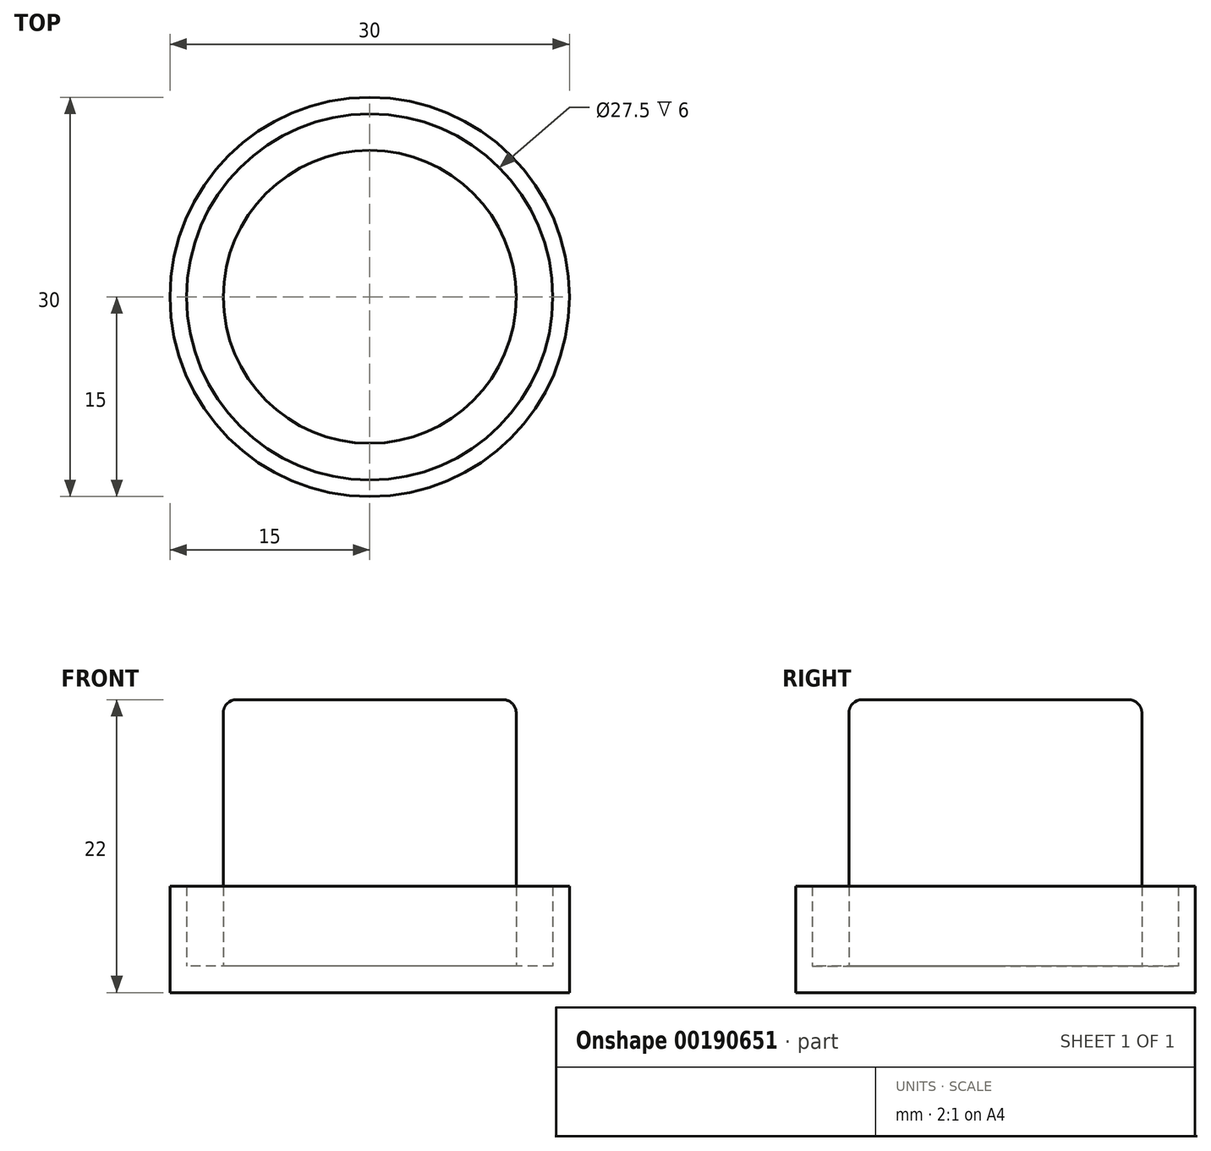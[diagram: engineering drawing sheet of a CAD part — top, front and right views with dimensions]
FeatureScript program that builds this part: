
annotation { "Feature Type Name" : "Feature", "Feature Type Description" : "" }
export const myFeature = defineFeature(function(context is Context, id is Id, definition is map)
    precondition{}
    {
        {
            var Q0;
            Q0=qCreatedBy(makeId("Top.planeOp"),FACE);
            var sketch = newSketch(context, id + "F0", { "sketchPlane" : qUnion([Q0])});
            skCircle(sketch, "E0", {"center": v(0, 0) * mm, "radius": 11 * mm});
            skCircle(sketch, "E1", {"center": v(0, 0) * mm, "radius": 13.75 * mm});
            skCircle(sketch, "E2", {"center": v(0, 0) * mm, "radius": 15 * mm});
            skSolve(sketch);
        }
        {
            var Q0;
            Q0=makeQuery(id+"F0.imprint","IMPRINT",FACE,{"disambiguationData":[TD([[makeQuery(id+"F0.imprint","IMPRINT",EDGE,{"derivedFrom":sQuery(id+"F0.wireOp",EDGE,"E1")}),-1.0]])]});
            extrude(context, id + "F1", {"entities" : qUnion([Q0]), "depth" : 6 * mm});
        }
        {
            var Q0;
            Q0 = qSketchRegion(id + "F0", true);
            var Q1;
            Q1=makeQuery(id+"F0.imprint","IMPRINT",FACE,{"disambiguationData":[TD([[makeQuery(id+"F0.imprint","IMPRINT",EDGE,{"derivedFrom":sQuery(id+"F0.wireOp",EDGE,"E0")}),-1.0]])]});
            var Q2;
            Q2=makeQuery(id+"F0.imprint","IMPRINT",FACE,{"disambiguationData":[TD([[makeQuery(id+"F0.imprint","IMPRINT",EDGE,{"derivedFrom":sQuery(id+"F0.wireOp",EDGE,"E0")}),1.0]])]});
            extrude(context, id + "F2", {"entities" : qUnion([Q0, Q1, Q2]), "operationType" : NewBodyOperationType.ADD, "oppositeDirection" : true, "depth" : 2 * mm});
        }
        {
            var Q0;
            Q0=makeQuery(id+"F0.imprint","IMPRINT",FACE,{"disambiguationData":[TD([[makeQuery(id+"F0.imprint","IMPRINT",EDGE,{"derivedFrom":sQuery(id+"F0.wireOp",EDGE,"E0")}),1.0]])]});
            extrude(context, id + "F3", {"entities" : qUnion([Q0]), "operationType" : NewBodyOperationType.ADD, "depth" : 20 * mm});
        }
        {
            var Q0;
            Q0=makeQuery(id+"F3.opExtrude","CAP_EDGE",EDGE,{"disambiguationData":[OSD([sQuery(id+"F0.wireOp",EDGE,"E0")])],"isStart":false});
            fillet(context, id + "F4", {"entities" : qUnion([Q0]), "radius" : 1 * mm, "tangentPropagation" : true, "allowEdgeOverflow" : false});
        }
    });
